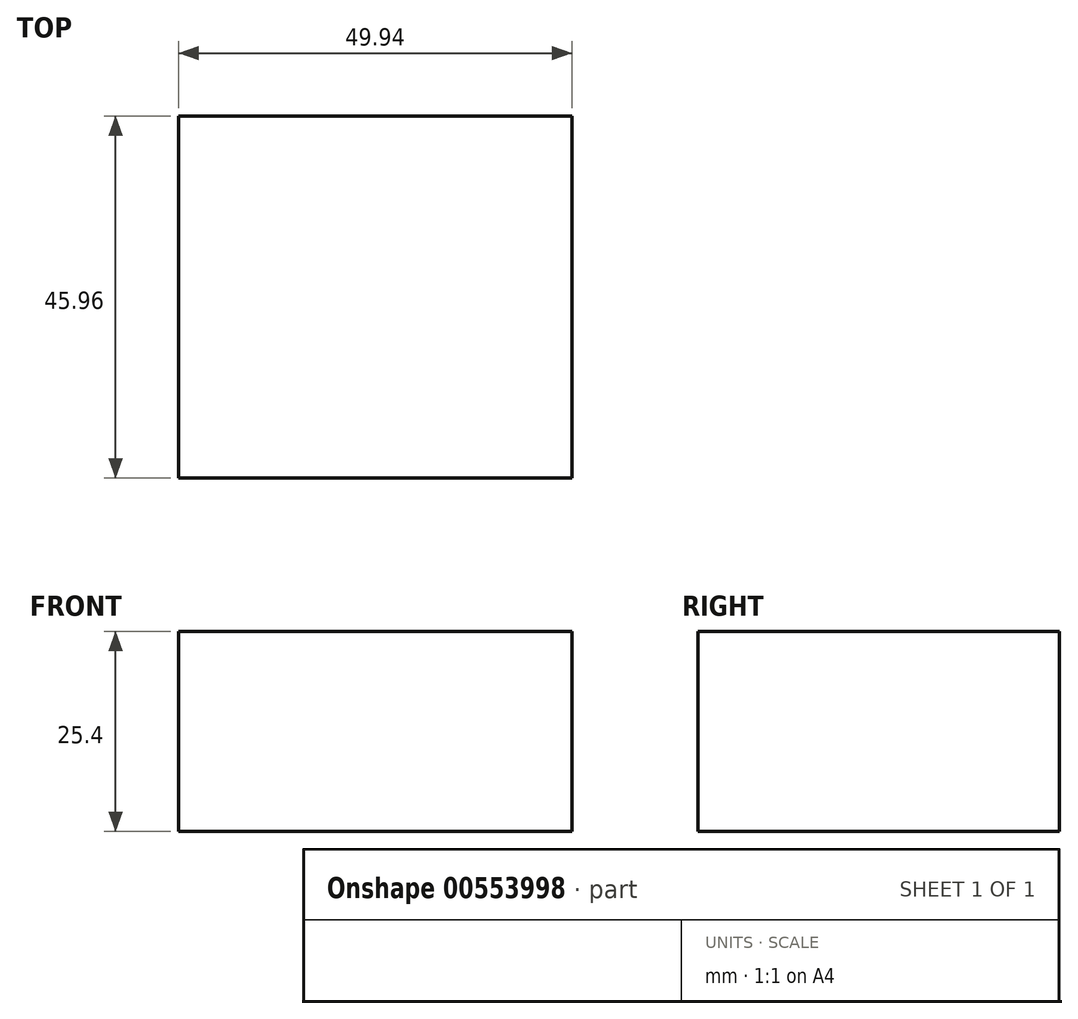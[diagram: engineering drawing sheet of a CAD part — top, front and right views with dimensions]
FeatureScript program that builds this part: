
annotation { "Feature Type Name" : "Feature", "Feature Type Description" : "" }
export const myFeature = defineFeature(function(context is Context, id is Id, definition is map)
    precondition{}
    {
        {
            var Q0;
            Q0=qCreatedBy(makeId("Top.planeOp"),FACE);
            var sketch = newSketch(context, id + "F0", { "sketchPlane" : qUnion([Q0])});
            skLineSegment(sketch, "E0.bottom", {"start": v(24.97, 22.98) * mm, "end": v(-24.97, 22.98) * mm});
            skLineSegment(sketch, "E0.top", {"start": v(24.97, -22.98) * mm, "end": v(-24.97, -22.98) * mm});
            skLineSegment(sketch, "E0.left", {"start": v(24.97, 22.98) * mm, "end": v(24.97, -22.98) * mm});
            skLineSegment(sketch, "E0.right", {"start": v(-24.97, 22.98) * mm, "end": v(-24.97, -22.98) * mm});
            skPoint(sketch, "E0.middle", {"position": v(0, 0) * mm});
            skSolve(sketch);
        }
        {
            var Q0;
            Q0=makeQuery(id+"F0.imprint","IMPRINT",FACE,{"disambiguationData":[TD([[makeQuery(id+"F0.imprint","IMPRINT",EDGE,{"derivedFrom":sQuery(id+"F0.wireOp",EDGE,"E0.bottom")}),1.0]])]});
            extrude(context, id + "F1", {"entities" : qUnion([Q0]), "depth" : 25.4 * mm, "offsetDistance" : 25.4 * mm});
        }
    });
